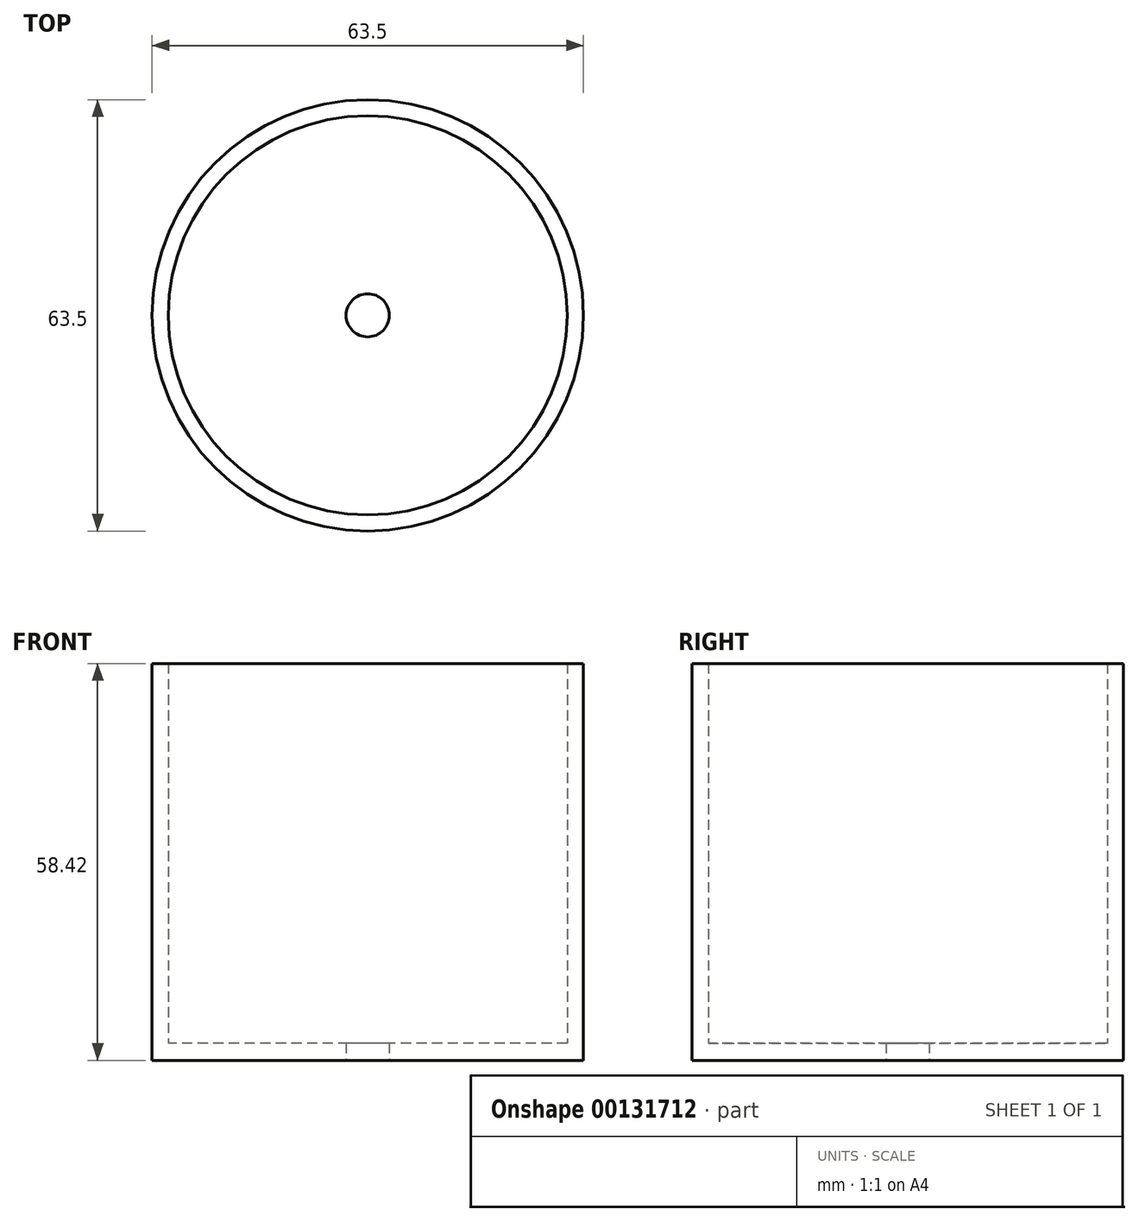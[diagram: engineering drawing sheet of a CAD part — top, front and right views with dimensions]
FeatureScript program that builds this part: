
annotation { "Feature Type Name" : "Feature", "Feature Type Description" : "" }
export const myFeature = defineFeature(function(context is Context, id is Id, definition is map)
    precondition{}
    {
        {
            var Q0;
            Q0=qCreatedBy(makeId("Top.planeOp"),FACE);
            var sketch = newSketch(context, id + "F0", { "sketchPlane" : qUnion([Q0])});
            skCircle(sketch, "E0", {"center": v(0, 0) * mm, "radius": 29.37 * mm});
            skSolve(sketch);
        }
        {
            var Q0;
            Q0=makeQuery(id+"F0.imprint","IMPRINT",FACE,{"disambiguationData":[TD([[makeQuery(id+"F0.imprint","IMPRINT",EDGE,{"derivedFrom":sQuery(id+"F0.wireOp",EDGE,"E0")}),1.0]])]});
            var sketch = newSketch(context, id + "F1", { "sketchPlane" : qUnion([Q0])});
            skCircle(sketch, "E1", {"center": v(0, 0) * mm, "radius": 31.75 * mm});
            skSolve(sketch);
        }
        {
            var Q0;
            Q0=makeQuery(id+"F1.imprint","IMPRINT",FACE,{"disambiguationData":[TD([[makeQuery(id+"F1.imprint","IMPRINT",EDGE,{"derivedFrom":sQuery(id+"F1.wireOp",EDGE,"E1")}),1.0]])]});
            extrude(context, id + "F2", {"entities" : qUnion([Q0]), "depth" : 58.42 * mm});
        }
        {
            var Q0;
            Q0=qCreatedBy(makeId("Top.planeOp"),FACE);
            var sketch = newSketch(context, id + "F3", { "sketchPlane" : qUnion([Q0])});
            skCircle(sketch, "E2", {"center": v(0, 0) * mm, "radius": 29.37 * mm});
            skSolve(sketch);
        }
        {
            var Q0;
            Q0=makeQuery(id+"F0.imprint","IMPRINT",FACE,{"disambiguationData":[TD([[makeQuery(id+"F0.imprint","IMPRINT",EDGE,{"derivedFrom":sQuery(id+"F0.wireOp",EDGE,"E0")}),1.0]])]});
            extrude(context, id + "F4", {"entities" : qUnion([Q0]), "operationType" : NewBodyOperationType.ADD, "depth" : 2.54 * mm});
        }
        {
            var Q0;
            Q0=makeQuery(id+"F3.imprint","IMPRINT",FACE,{"disambiguationData":[TD([[makeQuery(id+"F3.imprint","IMPRINT",EDGE,{"derivedFrom":sQuery(id+"F3.wireOp",EDGE,"E2")}),1.0]])]});
            var sketch = newSketch(context, id + "F5", { "sketchPlane" : qUnion([Q0])});
            skCircle(sketch, "E3", {"center": v(0, 0) * mm, "radius": 3.18 * mm});
            skSolve(sketch);
        }
        {
            var Q0;
            Q0=makeQuery(id+"F5.imprint","IMPRINT",FACE,{"disambiguationData":[TD([[makeQuery(id+"F5.imprint","IMPRINT",EDGE,{"derivedFrom":sQuery(id+"F5.wireOp",EDGE,"E3")}),1.0]])]});
            extrude(context, id + "F6", {"entities" : qUnion([Q0]), "operationType" : NewBodyOperationType.REMOVE, "endBound" : BoundingType.THROUGH_ALL, "depth" : 25.4 * mm});
        }
    });
